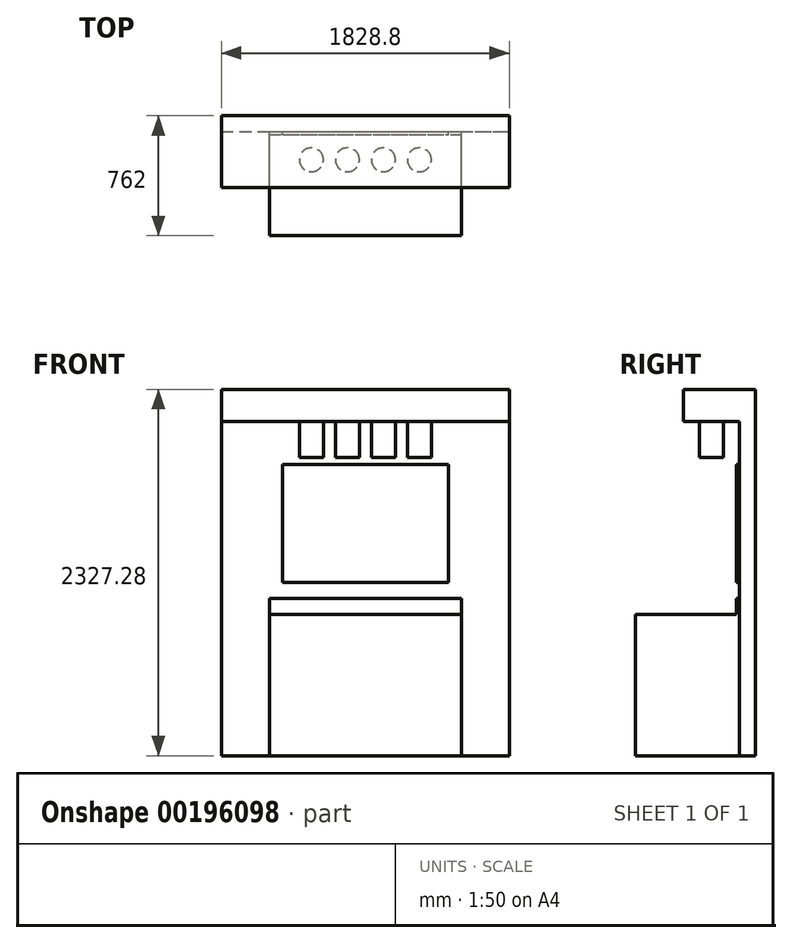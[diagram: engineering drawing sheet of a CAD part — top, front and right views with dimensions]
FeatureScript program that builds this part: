
annotation { "Feature Type Name" : "Feature", "Feature Type Description" : "" }
export const myFeature = defineFeature(function(context is Context, id is Id, definition is map)
    precondition{}
    {
        {
            var Q0;
            Q0=qCreatedBy(makeId("Front.planeOp"),FACE);
            var sketch = newSketch(context, id + "F0", { "sketchPlane" : qUnion([Q0])});
            skLineSegment(sketch, "E0.bottom", {"start": v(0, 0) * mm, "end": v(1828.8, 0) * mm});
            skLineSegment(sketch, "E0.top", {"start": v(0, 2133.6) * mm, "end": v(1828.8, 2133.6) * mm});
            skLineSegment(sketch, "E0.left", {"start": v(0, 0) * mm, "end": v(0, 2133.6) * mm});
            skLineSegment(sketch, "E0.right", {"start": v(1828.8, 0) * mm, "end": v(1828.8, 2133.6) * mm});
            skSolve(sketch);
        }
        {
            var Q0;
            Q0=makeQuery(id+"F0.imprint","IMPRINT",FACE,{"disambiguationData":[TD([[makeQuery(id+"F0.imprint","IMPRINT",EDGE,{"derivedFrom":sQuery(id+"F0.wireOp",EDGE,"E0.bottom")}),1.0]])]});
            extrude(context, id + "F1", {"entities" : qUnion([Q0]), "depth" : 101.6 * mm, "offsetDistance" : 25.4 * mm});
        }
        {
            var Q0;
            Q0=makeQuery(id+"F1.opExtrude","CAP_FACE",FACE,{"disambiguationData":[OSD([sQuery(id+"F0.wireOp",EDGE,"E0.bottom"),sQuery(id+"F0.wireOp",EDGE,"E0.top"),sQuery(id+"F0.wireOp",EDGE,"E0.left"),sQuery(id+"F0.wireOp",EDGE,"E0.right")])],"isStart":false});
            var sketch = newSketch(context, id + "F2", { "sketchPlane" : qUnion([Q0])});
            skLineSegment(sketch, "E1.bottom", {"start": v(304.8, 0) * mm, "end": v(1524, 0) * mm});
            skLineSegment(sketch, "E1.top", {"start": v(304.8, 898.53) * mm, "end": v(1524, 898.53) * mm});
            skLineSegment(sketch, "E1.left", {"start": v(304.8, 0) * mm, "end": v(304.8, 898.52) * mm});
            skLineSegment(sketch, "E1.right", {"start": v(1524, 0) * mm, "end": v(1524, 898.53) * mm});
            skLineSegment(sketch, "E2", {"start": v(914.4, 898.53) * mm, "end": v(914.4, 0) * mm, "construction": true});
            skSolve(sketch);
        }
        {
            var Q0;
            Q0 = qSketchRegion(id + "F2", true);
            extrude(context, id + "F3", {"entities" : qUnion([Q0]), "operationType" : NewBodyOperationType.ADD, "depth" : 660.4 * mm, "offsetDistance" : 25.4 * mm});
        }
        {
            var Q0;
            Q0=makeQuery(id+"F1.opExtrude","CAP_FACE",FACE,{"disambiguationData":[OSD([sQuery(id+"F0.wireOp",EDGE,"E0.bottom"),sQuery(id+"F0.wireOp",EDGE,"E0.top"),sQuery(id+"F0.wireOp",EDGE,"E0.left"),sQuery(id+"F0.wireOp",EDGE,"E0.right")])],"isStart":false});
            var sketch = newSketch(context, id + "F4", { "sketchPlane" : qUnion([Q0])});
            skLineSegment(sketch, "E3.bottom", {"start": v(304.8, 898.53) * mm, "end": v(1524, 898.53) * mm});
            skLineSegment(sketch, "E3.top", {"start": v(304.8, 1000.13) * mm, "end": v(1524, 1000.13) * mm});
            skLineSegment(sketch, "E3.left", {"start": v(304.8, 898.53) * mm, "end": v(304.8, 1000.13) * mm});
            skLineSegment(sketch, "E3.right", {"start": v(1524, 898.53) * mm, "end": v(1524, 1000.13) * mm});
            skSolve(sketch);
        }
        {
            var Q0;
            Q0 = qSketchRegion(id + "F4", true);
            extrude(context, id + "F5", {"entities" : qUnion([Q0]), "operationType" : NewBodyOperationType.ADD, "depth" : 19.05 * mm, "offsetDistance" : 25.4 * mm});
        }
        {
            var Q0;
            Q0=makeQuery(id+"F1.opExtrude","CAP_FACE",FACE,{"disambiguationData":[OSD([sQuery(id+"F0.wireOp",EDGE,"E0.bottom"),sQuery(id+"F0.wireOp",EDGE,"E0.top"),sQuery(id+"F0.wireOp",EDGE,"E0.left"),sQuery(id+"F0.wireOp",EDGE,"E0.right")])],"isStart":false});
            var sketch = newSketch(context, id + "F6", { "sketchPlane" : qUnion([Q0])});
            skLineSegment(sketch, "E4.bottom", {"start": v(0, 2133.6) * mm, "end": v(1828.8, 2133.6) * mm});
            skLineSegment(sketch, "E4.top", {"start": v(0, 2124.08) * mm, "end": v(1828.8, 2124.08) * mm});
            skLineSegment(sketch, "E4.left", {"start": v(0, 2133.6) * mm, "end": v(0, 2124.08) * mm});
            skLineSegment(sketch, "E4.right", {"start": v(1828.8, 2133.6) * mm, "end": v(1828.8, 2124.08) * mm});
            skSolve(sketch);
        }
        {
            var Q0;
            Q0 = qSketchRegion(id + "F6", true);
            extrude(context, id + "F7", {"entities" : qUnion([Q0]), "operationType" : NewBodyOperationType.REMOVE, "endBound" : BoundingType.THROUGH_ALL, "oppositeDirection" : true, "depth" : 25.4 * mm, "offsetDistance" : 25.4 * mm});
        }
        {
            var Q0;
            Q0=makeQuery(id+"F1.opExtrude","CAP_FACE",FACE,{"disambiguationData":[OSD([sQuery(id+"F0.wireOp",EDGE,"E0.bottom"),sQuery(id+"F0.wireOp",EDGE,"E0.top"),sQuery(id+"F0.wireOp",EDGE,"E0.left"),sQuery(id+"F0.wireOp",EDGE,"E0.right")])],"isStart":false});
            var sketch = newSketch(context, id + "F8", { "sketchPlane" : qUnion([Q0])});
            skLineSegment(sketch, "E5.bottom", {"start": v(387.35, 1851.03) * mm, "end": v(1441.45, 1851.03) * mm});
            skLineSegment(sketch, "E5.top", {"start": v(387.35, 1101.73) * mm, "end": v(1441.45, 1101.73) * mm});
            skLineSegment(sketch, "E5.left", {"start": v(387.35, 1851.03) * mm, "end": v(387.35, 1101.73) * mm});
            skLineSegment(sketch, "E5.right", {"start": v(1441.45, 1851.03) * mm, "end": v(1441.45, 1101.73) * mm});
            skLineSegment(sketch, "E6", {"start": v(914.4, 1101.73) * mm, "end": v(914.4, 1000.13) * mm, "construction": true});
            skSolve(sketch);
        }
        {
            var Q0;
            Q0 = qSketchRegion(id + "F8", true);
            extrude(context, id + "F9", {"entities" : qUnion([Q0]), "depth" : 19.05 * mm, "offsetDistance" : 25.4 * mm});
        }
        {
            var Q0;
            Q0=makeQuery(id+"F1.opExtrude","CAP_FACE",FACE,{"disambiguationData":[OSD([sQuery(id+"F0.wireOp",EDGE,"E0.bottom"),sQuery(id+"F0.wireOp",EDGE,"E0.top"),sQuery(id+"F0.wireOp",EDGE,"E0.left"),sQuery(id+"F0.wireOp",EDGE,"E0.right")])],"isStart":true});
            var sketch = newSketch(context, id + "F10", { "sketchPlane" : qUnion([Q0])});
            skLineSegment(sketch, "E7.bottom", {"start": v(0, 2124.08) * mm, "end": v(-1828.8, 2124.08) * mm});
            skLineSegment(sketch, "E7.top", {"start": v(0, 2327.27) * mm, "end": v(-1828.8, 2327.27) * mm});
            skLineSegment(sketch, "E7.left", {"start": v(0, 2124.08) * mm, "end": v(0, 2327.27) * mm});
            skLineSegment(sketch, "E7.right", {"start": v(-1828.8, 2124.08) * mm, "end": v(-1828.8, 2327.27) * mm});
            skSolve(sketch);
        }
        {
            var Q0;
            Q0 = qSketchRegion(id + "F10", true);
            extrude(context, id + "F11", {"entities" : qUnion([Q0]), "operationType" : NewBodyOperationType.ADD, "oppositeDirection" : true, "depth" : 457.2 * mm, "offsetDistance" : 25.4 * mm});
        }
        {
            var Q0;
            Q0=makeQuery(id+"F11.opExtrude","SWEPT_FACE",FACE,{"disambiguationData":[OSD([sQuery(id+"F10.wireOp",EDGE,"E7.bottom")])]});
            var sketch = newSketch(context, id + "F12", { "sketchPlane" : qUnion([Q0])});
            skLineSegment(sketch, "E8.bottom", {"start": v(1257.3, 203.2) * mm, "end": v(571.5, 203.2) * mm});
            skLineSegment(sketch, "E8.top", {"start": v(1257.3, 355.6) * mm, "end": v(571.5, 355.6) * mm});
            skLineSegment(sketch, "E8.left", {"start": v(1257.3, 203.2) * mm, "end": v(1257.3, 355.6) * mm});
            skLineSegment(sketch, "E8.right", {"start": v(571.5, 203.2) * mm, "end": v(571.5, 355.6) * mm});
            skPoint(sketch, "E8.middle", {"position": v(914.4, 279.4) * mm});
            skPoint(sketch, "E8.middle.positionSnap0", {"position": v(914.4, 101.6) * mm});
            skPoint(sketch, "E8.middle.positionSnap1", {"position": v(1828.8, 279.4) * mm});
            skPoint(sketch, "E8.centerSnap0", {"position": v(914.4, 101.6) * mm});
            skPoint(sketch, "E8.centerSnap1", {"position": v(1828.8, 279.4) * mm});
            skLineSegment(sketch, "E9.bottom", {"start": v(1028.7, 203.2) * mm, "end": v(800.1, 203.2) * mm});
            skLineSegment(sketch, "E9.top", {"start": v(1028.7, 355.6) * mm, "end": v(800.1, 355.6) * mm});
            skLineSegment(sketch, "E9.left", {"start": v(1028.7, 203.2) * mm, "end": v(1028.7, 355.6) * mm});
            skLineSegment(sketch, "E9.right", {"start": v(800.1, 203.2) * mm, "end": v(800.1, 355.6) * mm});
            skCircle(sketch, "E10", {"center": v(1257.3, 279.4) * mm, "radius": 76.2 * mm});
            skCircle(sketch, "E11", {"center": v(1028.7, 279.4) * mm, "radius": 76.2 * mm});
            skCircle(sketch, "E12", {"center": v(800.1, 279.4) * mm, "radius": 76.2 * mm});
            skCircle(sketch, "E13", {"center": v(571.5, 279.4) * mm, "radius": 76.2 * mm});
            skSolve(sketch);
        }
        {
            var Q0;
            {var subQ0=sQuery(id+"F12.wireOp",EDGE,"E8.right");Q0=makeQuery(id+"F12.imprint","IMPRINT",FACE,{"disambiguationData":[TD([[makeQuery(id+"F12.imprint","IMPRINT",EDGE,{"derivedFrom":subQ0}),1.0]])]});}
            var Q1;
            {var subQ0=sQuery(id+"F12.wireOp",EDGE,"E9.right");Q1=makeQuery(id+"F12.imprint","IMPRINT",FACE,{"disambiguationData":[TD([[makeQuery(id+"F12.imprint","IMPRINT",EDGE,{"derivedFrom":subQ0}),1.0]])]});}
            var Q2;
            {var subQ0=sQuery(id+"F12.wireOp",EDGE,"E9.left");Q2=makeQuery(id+"F12.imprint","IMPRINT",FACE,{"disambiguationData":[TD([[makeQuery(id+"F12.imprint","IMPRINT",EDGE,{"derivedFrom":subQ0}),-1.0]])]});}
            var Q3;
            {var subQ0=sQuery(id+"F12.wireOp",EDGE,"E9.left");Q3=makeQuery(id+"F12.imprint","IMPRINT",FACE,{"disambiguationData":[TD([[makeQuery(id+"F12.imprint","IMPRINT",EDGE,{"derivedFrom":subQ0}),1.0]])]});}
            var Q4;
            {var subQ0=sQuery(id+"F12.wireOp",EDGE,"E9.right");Q4=makeQuery(id+"F12.imprint","IMPRINT",FACE,{"disambiguationData":[TD([[makeQuery(id+"F12.imprint","IMPRINT",EDGE,{"derivedFrom":subQ0}),-1.0]])]});}
            var Q5;
            {var subQ0=sQuery(id+"F12.wireOp",EDGE,"E8.right");Q5=makeQuery(id+"F12.imprint","IMPRINT",FACE,{"disambiguationData":[TD([[makeQuery(id+"F12.imprint","IMPRINT",EDGE,{"derivedFrom":subQ0}),-1.0]])]});}
            var Q6;
            {var subQ0=sQuery(id+"F12.wireOp",EDGE,"E8.left");Q6=makeQuery(id+"F12.imprint","IMPRINT",FACE,{"disambiguationData":[TD([[makeQuery(id+"F12.imprint","IMPRINT",EDGE,{"derivedFrom":subQ0}),1.0]])]});}
            var Q7;
            {var subQ0=sQuery(id+"F12.wireOp",EDGE,"E8.left");Q7=makeQuery(id+"F12.imprint","IMPRINT",FACE,{"disambiguationData":[TD([[makeQuery(id+"F12.imprint","IMPRINT",EDGE,{"derivedFrom":subQ0}),-1.0]])]});}
            extrude(context, id + "F13", {"entities" : qUnion([Q0, Q1, Q2, Q3, Q4, Q5, Q6, Q7]), "operationType" : NewBodyOperationType.ADD, "depth" : 228.6 * mm, "offsetDistance" : 25.4 * mm});
        }
    });
